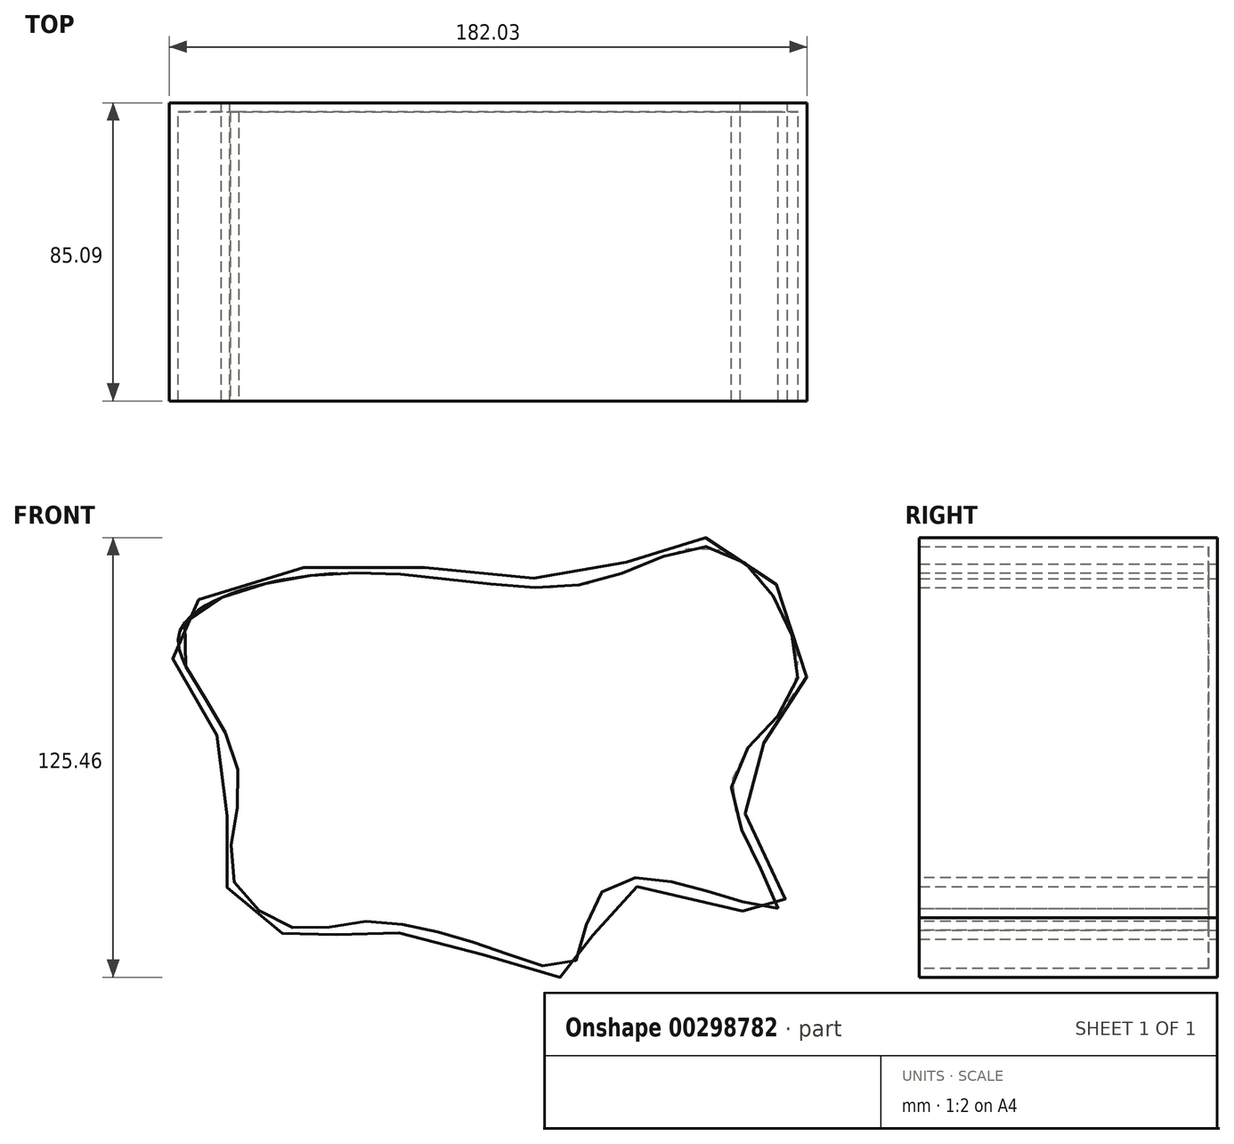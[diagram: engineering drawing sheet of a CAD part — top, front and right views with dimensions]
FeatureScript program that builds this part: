
annotation { "Feature Type Name" : "Feature", "Feature Type Description" : "" }
export const myFeature = defineFeature(function(context is Context, id is Id, definition is map)
    precondition{}
    {
        {
            var Q0;
            Q0=qCreatedBy(makeId("Front.planeOp"),FACE);
            var sketch = newSketch(context, id + "F0", { "sketchPlane" : qUnion([Q0])});
            skFitSpline(sketch, "E0", {"points": [v(0, -58.12) * mm, v(-36.48, -51.3) * mm, v(-52, -53.42) * mm, v(-73.9, -36.95) * mm, v(-72.95, -3.3) * mm, v(-89.42, 33.42) * mm, v(-38.83, 53.42) * mm, v(30.6, 50.6) * mm, v(69.66, 59.77) * mm, v(91.78, 17.88) * mm, v(73.42, -10.59) * mm, v(86.13, -46.83) * mm, v(39.06, -39.53) * mm, v(27.77, -62.36) * mm, v(0, -58.12) * mm]});
            skSolve(sketch);
        }
        {
            var Q0;
            Q0=makeQuery(id+"F0.imprint","IMPRINT",FACE,{"disambiguationData":[TD([[makeQuery(id+"F0.imprint","IMPRINT",EDGE,{"derivedFrom":sQuery(id+"F0.wireOp",EDGE,"E0")}),-1.0]])]});
            extrude(context, id + "F1", {"entities" : qUnion([Q0]), "depth" : 85.1 * mm});
        }
        {
            var Q0;
            Q0=makeQuery(id+"F1.opExtrude","CAP_FACE",FACE,{"disambiguationData":[OSD([sQuery(id+"F0.wireOp",EDGE,"E0")])],"isStart":false});
            shell(context, id + "F2", {"entities" : qUnion([Q0]), "thickness" : 2.54 * mm});
        }
    });
